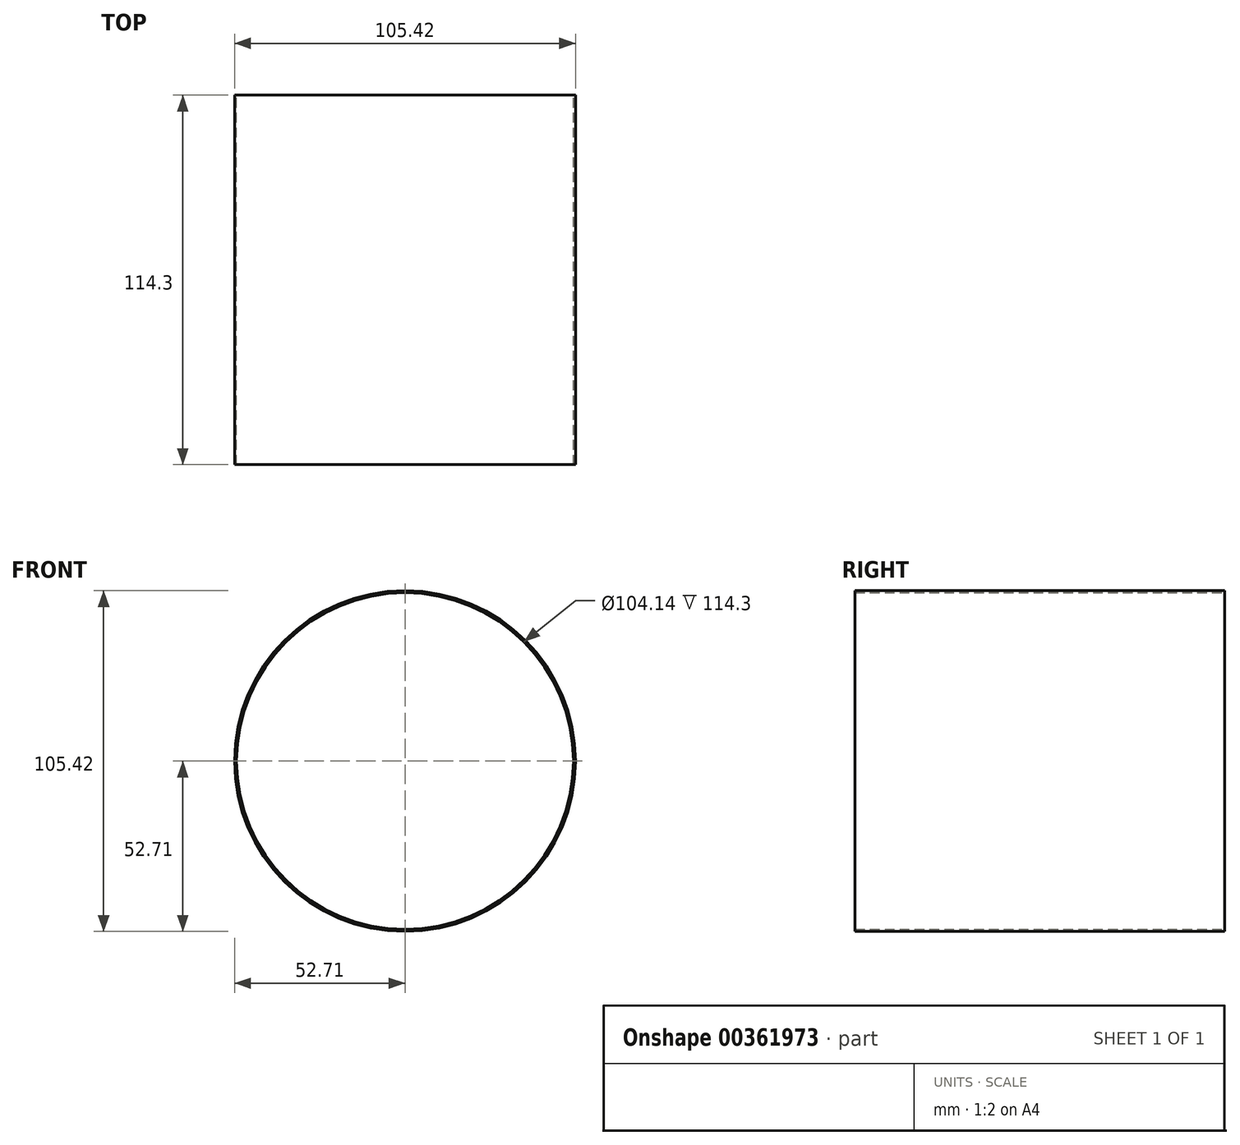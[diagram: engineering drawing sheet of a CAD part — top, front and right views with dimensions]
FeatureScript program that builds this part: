
annotation { "Feature Type Name" : "Feature", "Feature Type Description" : "" }
export const myFeature = defineFeature(function(context is Context, id is Id, definition is map)
    precondition{}
    {
        {
            var Q0;
            Q0=qCreatedBy(makeId("Front.planeOp"),FACE);
            var sketch = newSketch(context, id + "F0", { "sketchPlane" : qUnion([Q0])});
            skCircle(sketch, "E0", {"center": v(0, 0) * mm, "radius": 52.07 * mm});
            skCircle(sketch, "E1", {"center": v(0, 0) * mm, "radius": 52.7 * mm});
            skSolve(sketch);
        }
        {
            var Q0;
            Q0 = qSketchRegion(id + "F0", true);
            extrude(context, id + "F1", {"entities" : qUnion([Q0]), "endBound" : BoundingType.SYMMETRIC, "depth" : 114.3 * mm});
        }
    });
